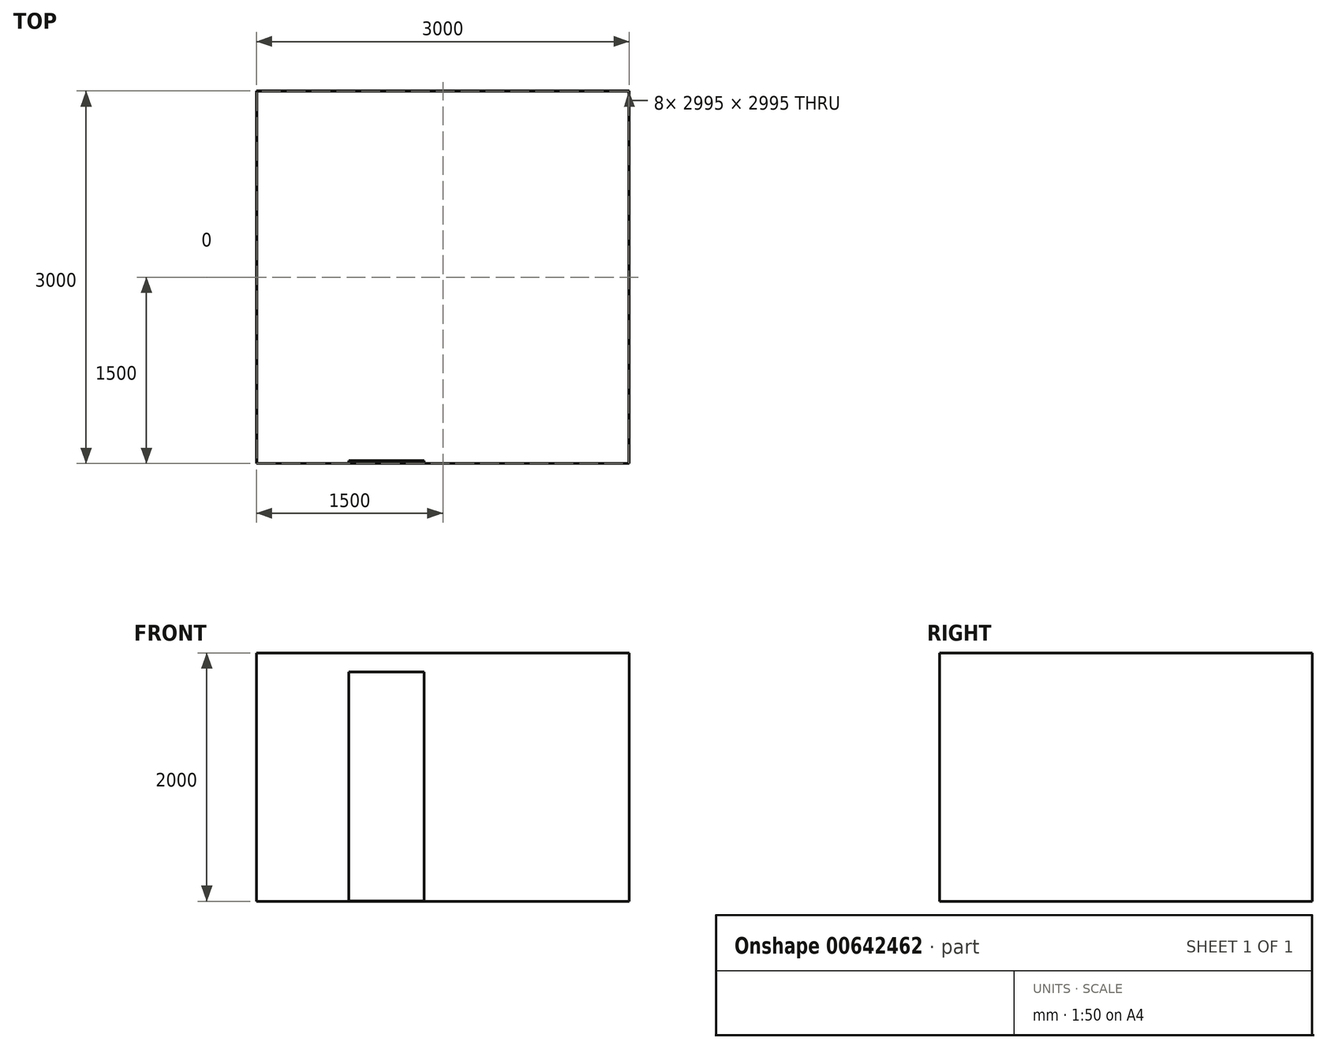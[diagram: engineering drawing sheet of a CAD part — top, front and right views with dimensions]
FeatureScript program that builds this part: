
annotation { "Feature Type Name" : "Feature", "Feature Type Description" : "" }
export const myFeature = defineFeature(function(context is Context, id is Id, definition is map)
    precondition{}
    {
        {
            var Q0;
            Q0=qCreatedBy(makeId("Top.planeOp"),FACE);
            var sketch = newSketch(context, id + "F0", { "sketchPlane" : qUnion([Q0])});
            skLineSegment(sketch, "E0.bottom", {"start": v(1500, 1500) * mm, "end": v(-1500, 1500) * mm});
            skLineSegment(sketch, "E0.top", {"start": v(1500, -1500) * mm, "end": v(-1500, -1500) * mm});
            skLineSegment(sketch, "E0.left", {"start": v(1500, 1500) * mm, "end": v(1500, -1500) * mm});
            skLineSegment(sketch, "E0.right", {"start": v(-1500, 1500) * mm, "end": v(-1500, -1500) * mm});
            skPoint(sketch, "E0.middle", {"position": v(0, 0) * mm});
            skSolve(sketch);
        }
        {
            var Q0;
            Q0=makeQuery(id+"F0.imprint","IMPRINT",FACE,{"disambiguationData":[TD([[makeQuery(id+"F0.imprint","IMPRINT",EDGE,{"derivedFrom":sQuery(id+"F0.wireOp",EDGE,"E0.bottom")}),1.0]])]});
            extrude(context, id + "F1", {"entities" : qUnion([Q0]), "depth" : 2000 * mm, "offsetDistance" : 25 * mm});
        }
        {
            var Q0;
            Q0=makeQuery(id+"F1.opExtrude","CAP_FACE",FACE,{"disambiguationData":[OSD([sQuery(id+"F0.wireOp",EDGE,"E0.bottom"),sQuery(id+"F0.wireOp",EDGE,"E0.top"),sQuery(id+"F0.wireOp",EDGE,"E0.left"),sQuery(id+"F0.wireOp",EDGE,"E0.right")])],"isStart":false});
            shell(context, id + "F2", {"entities" : qUnion([Q0]), "thickness" : 2.5 * mm});
        }
        {
            var Q0;
            Q0=makeQuery(id+"F1.opExtrude","SWEPT_FACE",FACE,{"disambiguationData":[OSD([sQuery(id+"F0.wireOp",EDGE,"E0.top")])]});
            var sketch = newSketch(context, id + "F3", { "sketchPlane" : qUnion([Q0])});
            skLineSegment(sketch, "E1.bottom", {"start": v(-757.75, 0) * mm, "end": v(-150.34, 0) * mm});
            skLineSegment(sketch, "E1.top", {"start": v(-757.75, 1847.02) * mm, "end": v(-150.34, 1847.02) * mm});
            skLineSegment(sketch, "E1.left", {"start": v(-757.75, 0) * mm, "end": v(-757.75, 1847.02) * mm});
            skLineSegment(sketch, "E1.right", {"start": v(-150.34, 0) * mm, "end": v(-150.34, 1847.02) * mm});
            skSolve(sketch);
        }
        {
            var Q0;
            Q0 = qSketchRegion(id + "F3", true);
            extrude(context, id + "F4", {"entities" : qUnion([Q0]), "operationType" : NewBodyOperationType.REMOVE, "oppositeDirection" : true, "depth" : 25 * mm, "offsetDistance" : 25 * mm});
        }
    });
